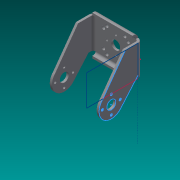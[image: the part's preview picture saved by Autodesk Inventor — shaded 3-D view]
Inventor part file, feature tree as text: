
AUTODESK INVENTOR PART (.ipt)
format: ipt  version: 2013 SP2 (Build 170200200, 200)  size: 262,656 bytes
history: native  units: mm
features: sheet_metal_op x15, sketch x11, other x9, plane x1, mirror x1
ambient origin geometry x8: Origin, YZ Plane, XZ Plane, XY Plane, X Axis, Y Axis, Z Axis, Center Point
bodies: Solid1 (feature_tree)
feature tree (37):
  sheet_metal_op  "Face1"
  sheet_metal_op  "Flange3"
  sheet_metal_op  "Flange4"
  sketch  "Sketch6"  dims[d23=2.0mm]
  sheet_metal_op  "Face2"
  sketch  "Sketch7"  dims[d24=1.0mm]
  plane  "Work Plane1"
  mirror  "Mirror1"
  sketch  "Sketch9"  dims[d26=2.0mm]
  sketch  "Sketch10"  dims[d27=50.0mm d28=90.0deg d29=2.0mm]
  sheet_metal_op  "Flange5"
  sheet_metal_op  "Flange6"
  sketch  "Sketch1"  dims[d0=36.0mm]
  other  "Plate1"
  sketch  "Sketch4"  dims[d1=27.5mm]
  other  "Plate4"
  sheet_metal_op  "Bend3"
  sheet_metal_op  "Corner3"
  sketch  "Sketch5"  dims[d2=2.0mm]
  other  "Plate5"
  sheet_metal_op  "Bend4"
  sheet_metal_op  "Corner4"
  other  "Plate6"
  sheet_metal_op  "Bend5"
  sketch  "Sketch8"  dims[d25=4.0mm]
  sketch  "Sketch11"  dims[d30=8.0mm]
  sketch  "Sketch12"  dims[d31=2.0mm]
  other  "Plate7"
  sheet_metal_op  "Bend6"
  sheet_metal_op  "Corner5"
  sketch  "Sketch13"  dims[d32=2.0mm d33=2.0mm d34=1.0mm d35=4.0mm d36=2.0mm d37=50.0mm d38=90.0deg d39=2.0mm d40=8.0mm d41=2.0mm d42=2.0mm d46=2.0mm d47=2.0mm d48=1.0mm d49=4.0mm d50=2.0mm d51=2.0mm d52=0.0mm d53=90.0deg d54=2.0mm d55=0.0mm d62=16.0mm d63=22.0mm d64=3.0mm d65=3.0mm d66=3.0mm d67=3.0mm d68=2.0mm d69=0.0mm d70=2.0mm d71=1.0mm d72=4.0mm d73=2.0mm d74=5.0mm d75=90.0deg d76=2.0mm d77=8.0mm d78=2.0mm d79=2.0mm d80=2.0mm d81=1.0mm d82=4.0mm d83=2.0mm d84=5.0mm d85=90.0deg d86=2.0mm d87=8.0mm d88=2.0mm d89=2.0mm]
  other  "Plate8"
  sheet_metal_op  "Bend7"
  sheet_metal_op  "Corner6"
  other  "Cut1"
  other  "Cut2"
  other  "Cut3"
